# Revit family: Urinal-Flush_Actuator_Sensor-KOHLER-Mini-K-8872T
name_source: partatom
category: Specialty Equipment
units: mm (PartAtom-declared; Revit-internal decimal feet)

## family parameters
Cut with Voids When Loaded = No
Host = Face
OmniClass Number = 23.31.25.00
OmniClass Title = Toilet and Bath Specialties
Part Type = Normal
Room Calculation Point = No
Round Connector Dimension = Use Diameter
Shared = No

## types (2) — shared parameters
ADA Compliant = No
Apparent Load = 0 VA
Assembly Code = C1030200
Date Modified = 09/28/2023
Default Elevation = 42"
Electrical Connector = Yes
Electrical Note = One Dedicated Circuit Required
Finish = Kohler-Metal-CP-Polished_Chrome
Height = 2 3/16"
Length = 2 1/2"
Manufacturer = Kohler Co.
Master Format 2014 = 10 28 00
Master Format 2014 Name = Toilet, Bath, and Laundry Accessories
Material = Premium Metal Construction
Product Name = Mini
URL = http://www.kohler.com.cn
Voltage = 220 V
WaterSense Certified = No
Width = 2 3/16"

## per-type parameters (varying)
| type | Description | Model | Type |
| 2W, CP-Polished Chrome | Urinal Sensor 0.5 LPF/1 LPF | K-8872T-2W-CP | 1 |
| 2, CP-Polished Chrome | Urinal Sensor 2.5 LPF | K-8872T-2-CP | 2 |

## geometry (parser evidence)
native form markers: Sweep x4
no freeform markers — native parametric forms only
